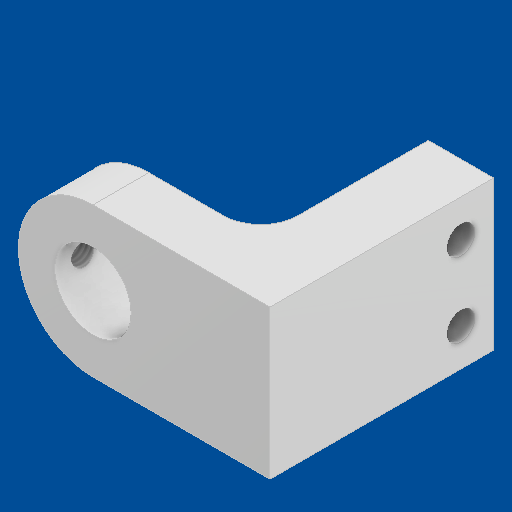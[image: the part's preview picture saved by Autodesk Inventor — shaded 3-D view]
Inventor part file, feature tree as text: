
AUTODESK INVENTOR PART (.ipt)
format: ipt  version: 2025 (Build 290162000, 162)  size: 216,064 bytes
history: native  units: in
note: dims shown in document units (in); Inventor stores cm internally (conversion verified against a paired STEP export)
features: direct_edit x11, move_body x8, other x6, hole x1, sketch x1
ambient origin geometry x8: Origin, YZ Plane, XZ Plane, XY Plane, X Axis, Y Axis, Z Axis, Center Point
bodies: Solid1 (feature_tree), Body3 (feature_tree)
feature tree (27):
  move_body  "Move Body1"
  direct_edit  "Direct Edit1"
  direct_edit  "Direct Edit2"
  direct_edit  "Direct Edit3"
  hole  "Hole1"  [1 undecoded]
  direct_edit  "Direct Edit4"
  direct_edit  "Direct Edit5"
  direct_edit  "Direct Edit6"
  direct_edit  "Direct Edit7"
  direct_edit  "Direct Edit8"
  direct_edit  "Direct Edit9"
  direct_edit  "Direct Edit10"
  direct_edit  "Direct Edit11"
  sketch  "Sketch1"  dims[d0=45.0deg d1=0.0059in d2=0.0625in d3=0.0625in d4=0.1181in d5=0.0in d6=0.0089in d7=90.0deg d8=0.0968in d9=0.2362in d10=0.1575in d11=0.0787in d12=90.0deg d13=0.3465in d14=0.8108in d15=0.0039in d16=0.0039in d17=0.0in d18=0.0in d19=-0.0295in d20=0.0in d21=0.0in d22=-0.0089in d23=0.0in d24=0.0in d25=-0.0089in d26=-0.0039in d27=0.0016in d28=0.0in d29=0.0in d30=-0.0083in d31=0.0in d32=0.0in d33=0.0in d34=0.0055in d35=0.0in d36=-0.0002in d37=0.0in d38=0.0in]
  other  "Size1"
  other  "Size2"
  other  "Size3"
  other  "Size4"
  other  "Size5"
  move_body  "Move1"
  move_body  "Move2"
  move_body  "Move3"
  other  "Size6"
  move_body  "Move4"
  move_body  "Move5"
  move_body  "Move6"
  move_body  "Move7"
note: 1 required parameter value undecoded (feature->parameter linkage not recoverable at this tier; creation-order binding heuristic only, values carry confidence <= 0.55)
